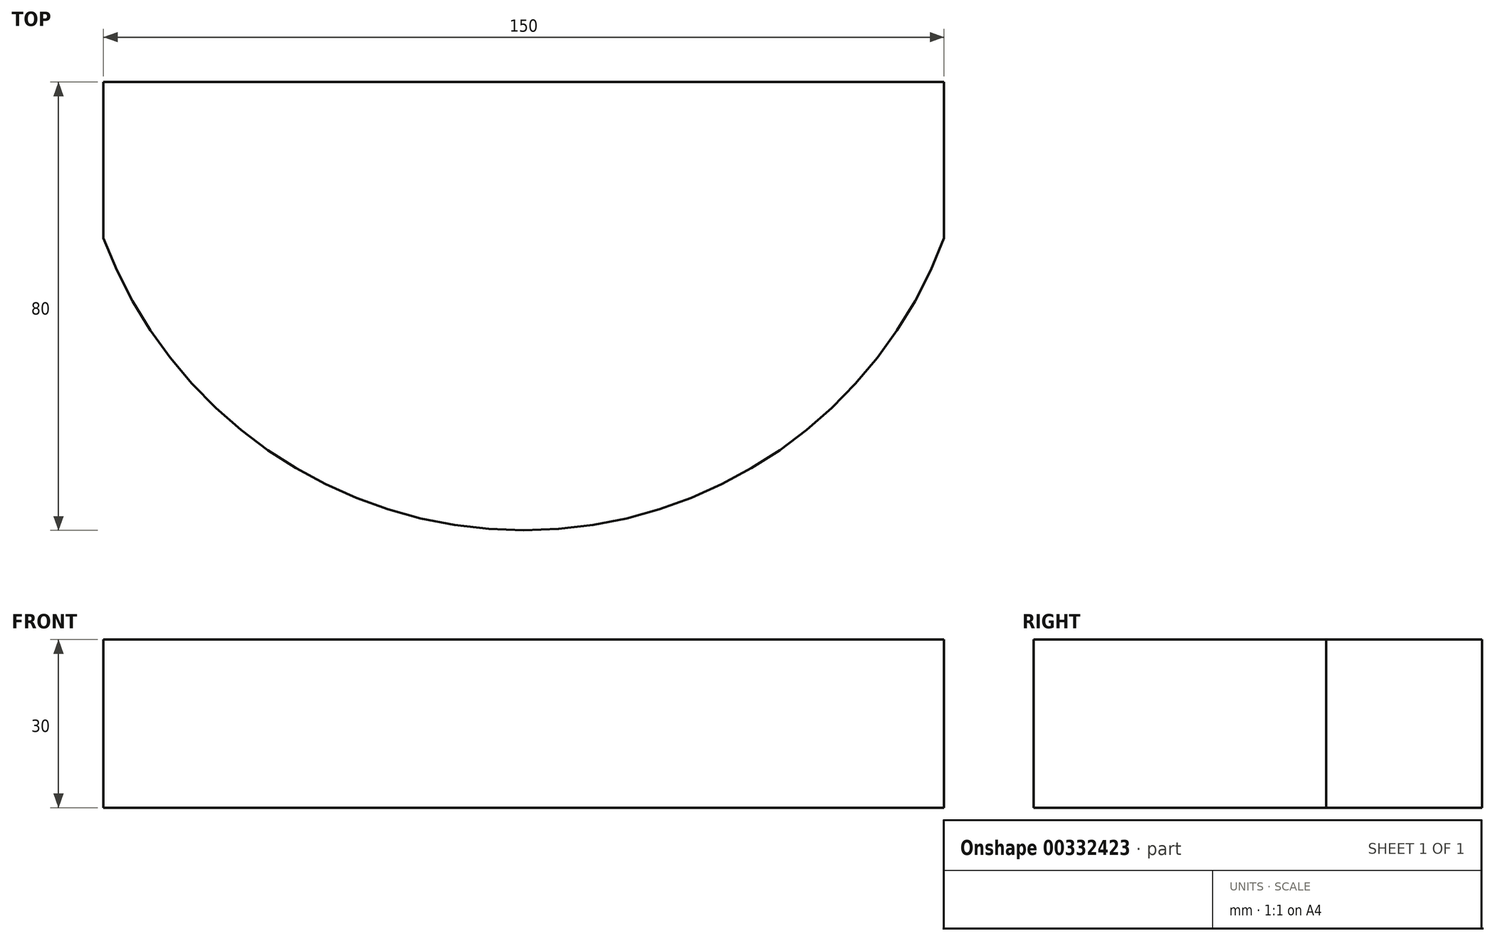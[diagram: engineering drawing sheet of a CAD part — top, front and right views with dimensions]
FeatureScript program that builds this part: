
annotation { "Feature Type Name" : "Feature", "Feature Type Description" : "" }
export const myFeature = defineFeature(function(context is Context, id is Id, definition is map)
    precondition{}
    {
        {
            var Q0;
            Q0=qCreatedBy(makeId("Top.planeOp"),FACE);
            var sketch = newSketch(context, id + "F0", { "sketchPlane" : qUnion([Q0])});
            skArc(sketch, "E0", {"start": v(-75, -27.84) * mm, "mid": v(0, -80) * mm, "end": v(75, -27.84) * mm});
            skLineSegment(sketch, "E1", {"start": v(0, 0) * mm, "end": v(-75, 0) * mm});
            skLineSegment(sketch, "E2", {"start": v(0, 0) * mm, "end": v(75, 0) * mm});
            skLineSegment(sketch, "E3", {"start": v(-75, 0) * mm, "end": v(-75, -27.84) * mm});
            skLineSegment(sketch, "E4", {"start": v(75, 0) * mm, "end": v(75, -27.84) * mm});
            skSolve(sketch);
        }
        {
            var Q0;
            Q0=makeQuery(id+"F0.imprint","IMPRINT",FACE,{"disambiguationData":[TD([[makeQuery(id+"F0.imprint","IMPRINT",EDGE,{"derivedFrom":sQuery(id+"F0.wireOp",EDGE,"E0")}),1.0]])]});
            extrude(context, id + "F1", {"entities" : qUnion([Q0]), "depth" : 30 * mm});
        }
    });
